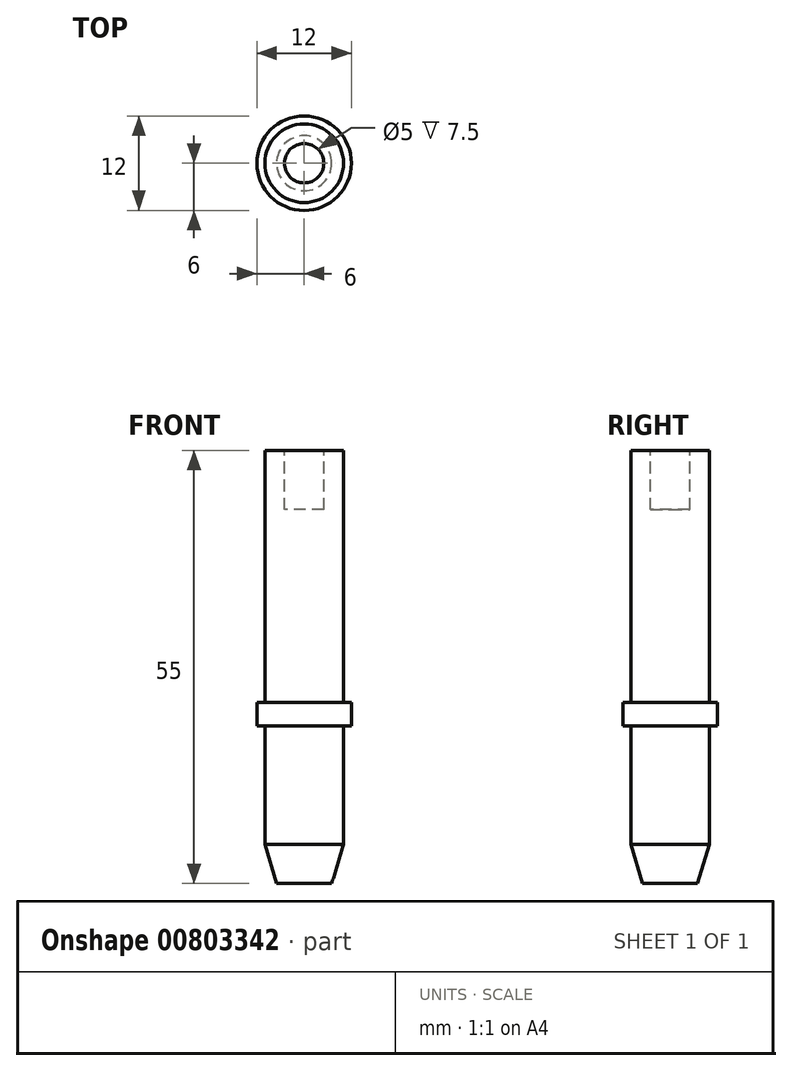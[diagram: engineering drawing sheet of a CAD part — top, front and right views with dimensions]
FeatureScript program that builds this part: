
annotation { "Feature Type Name" : "Feature", "Feature Type Description" : "" }
export const myFeature = defineFeature(function(context is Context, id is Id, definition is map)
    precondition{}
    {
        {
            var Q0;
            Q0=qCreatedBy(makeId("Front.planeOp"),FACE);
            var sketch = newSketch(context, id + "F0", { "sketchPlane" : qUnion([Q0])});
            skLineSegment(sketch, "E0.bottom", {"start": v(2.5, 0) * mm, "end": v(5, 0) * mm});
            skLineSegment(sketch, "E0.top", {"start": v(0, -50) * mm, "end": v(5, -50) * mm});
            skLineSegment(sketch, "E0.left", {"start": v(0, -7.5) * mm, "end": v(0, -50) * mm});
            skLineSegment(sketch, "E0.right", {"start": v(5, 0) * mm, "end": v(5, -32) * mm});
            skLineSegment(sketch, "E1.top", {"start": v(0, -7.5) * mm, "end": v(2.5, -7.5) * mm});
            skLineSegment(sketch, "E1.right", {"start": v(2.5, 0) * mm, "end": v(2.5, -7.5) * mm});
            skLineSegment(sketch, "E2.bottom", {"start": v(0, -50) * mm, "end": v(3.5, -50) * mm});
            skLineSegment(sketch, "E2.top", {"start": v(0, -55) * mm, "end": v(3.5, -55) * mm});
            skLineSegment(sketch, "E2.left", {"start": v(0, -50) * mm, "end": v(0, -55) * mm});
            skLineSegment(sketch, "E3", {"start": v(5, -50) * mm, "end": v(3.5, -55) * mm});
            skLineSegment(sketch, "E4.bottom", {"start": v(5, -32) * mm, "end": v(6, -32) * mm});
            skLineSegment(sketch, "E4.top", {"start": v(5, -35) * mm, "end": v(6, -35) * mm});
            skLineSegment(sketch, "E4.left", {"start": v(0, -32) * mm, "end": v(0, -35) * mm});
            skLineSegment(sketch, "E4.right", {"start": v(6, -32) * mm, "end": v(6, -35) * mm});
            skLineSegment(sketch, "E5.trimOffspring", {"start": v(5, -35) * mm, "end": v(5, -50) * mm});
            skSolve(sketch);
        }
        {
            var Q0;
            Q0 = qSketchRegion(id + "F0", true);
            var Q1;
            Q1=sQuery(id+"F0.wireOp",EDGE,"E0.left");
            revolve(context, id + "F1", {"surfaceOperationType" : NewSurfaceOperationType.NEW, "entities" : qUnion([Q0]), "axis" : qUnion([Q1]), "revolveType" : RevolveType.FULL});
        }
    });
